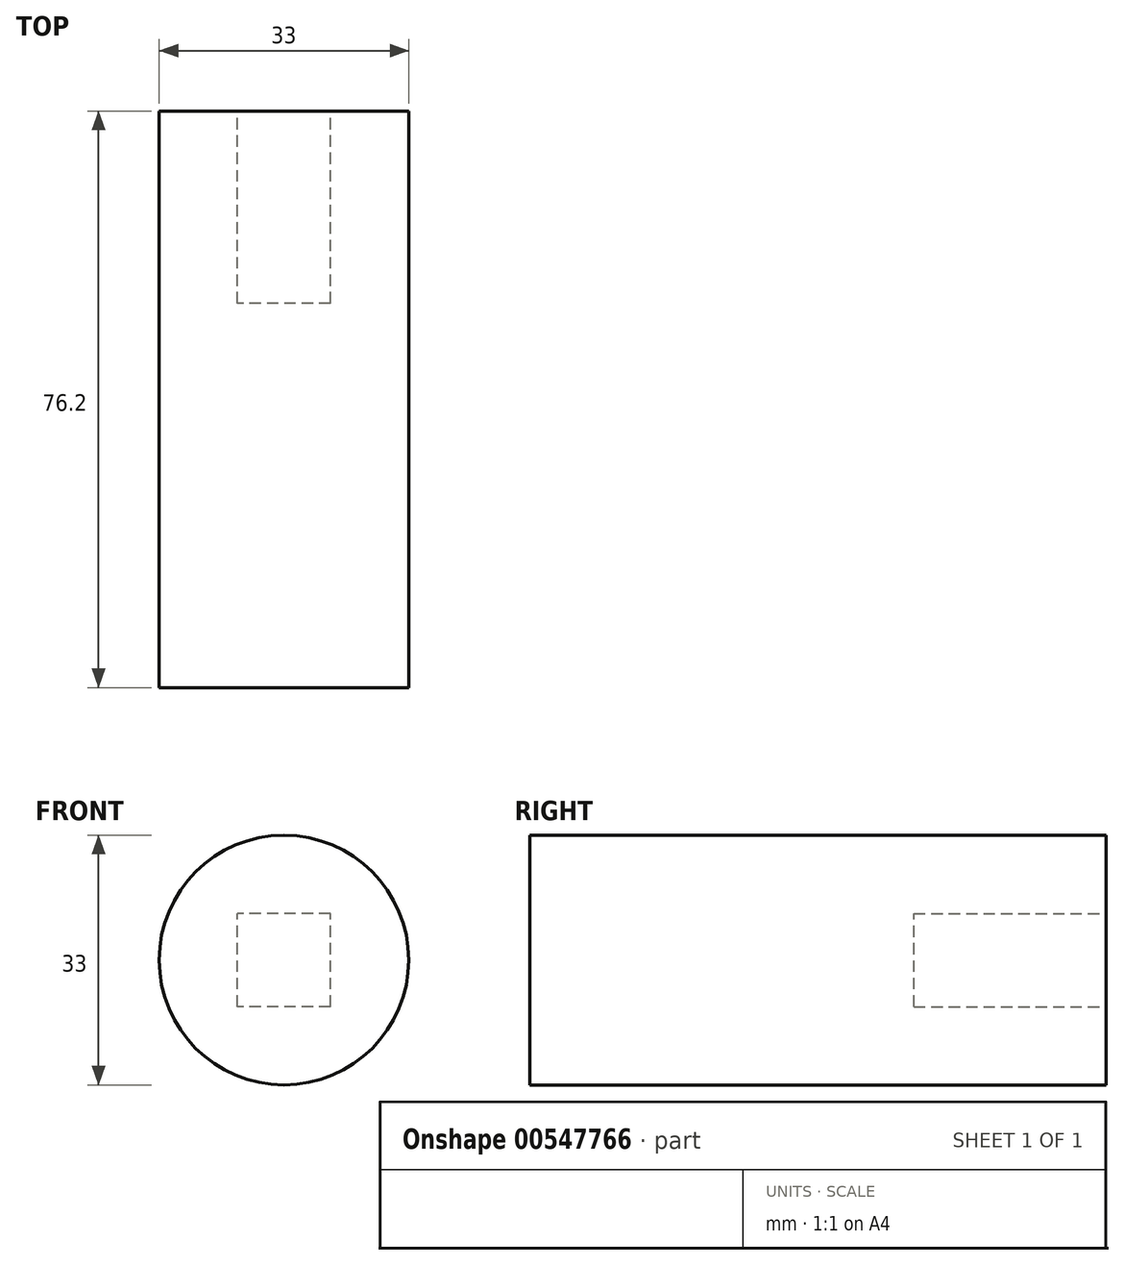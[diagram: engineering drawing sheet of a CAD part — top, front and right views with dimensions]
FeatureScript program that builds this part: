
annotation { "Feature Type Name" : "Feature", "Feature Type Description" : "" }
export const myFeature = defineFeature(function(context is Context, id is Id, definition is map)
    precondition{}
    {
        {
            var Q0;
            Q0=qCreatedBy(makeId("Front.planeOp"),FACE);
            var sketch = newSketch(context, id + "F0", { "sketchPlane" : qUnion([Q0])});
            skCircle(sketch, "E0", {"center": v(0, 0) * mm, "radius": 16.5 * mm});
            skLineSegment(sketch, "E1.bottom", {"start": v(6.15, -6.15) * mm, "end": v(-6.15, -6.15) * mm});
            skLineSegment(sketch, "E1.top", {"start": v(6.15, 6.15) * mm, "end": v(-6.15, 6.15) * mm});
            skLineSegment(sketch, "E1.left", {"start": v(6.15, -6.15) * mm, "end": v(6.15, 6.15) * mm});
            skLineSegment(sketch, "E1.right", {"start": v(-6.15, -6.15) * mm, "end": v(-6.15, 6.15) * mm});
            skSolve(sketch);
        }
        {
            var Q0;
            Q0 = qSketchRegion(id + "F0", true);
            extrude(context, id + "F1", {"entities" : qUnion([Q0]), "depth" : 25.4 * mm, "offsetDistance" : 25.4 * mm});
        }
        {
            var Q0;
            Q0=makeQuery(id+"F1.opExtrude","CAP_FACE",FACE,{"disambiguationData":[OSD([sQuery(id+"F0.wireOp",EDGE,"E0"),sQuery(id+"F0.wireOp",EDGE,"E1.bottom"),sQuery(id+"F0.wireOp",EDGE,"E1.top"),sQuery(id+"F0.wireOp",EDGE,"E1.left"),sQuery(id+"F0.wireOp",EDGE,"E1.right")])],"isStart":false});
            var sketch = newSketch(context, id + "F2", { "sketchPlane" : qUnion([Q0])});
            skCircle(sketch, "E2", {"center": v(0, 0) * mm, "radius": 16.5 * mm});
            skSolve(sketch);
        }
        {
            var Q0;
            Q0 = qSketchRegion(id + "F2", true);
            extrude(context, id + "F3", {"entities" : qUnion([Q0]), "operationType" : NewBodyOperationType.ADD, "depth" : 50.8 * mm, "offsetDistance" : 25.4 * mm});
        }
    });
